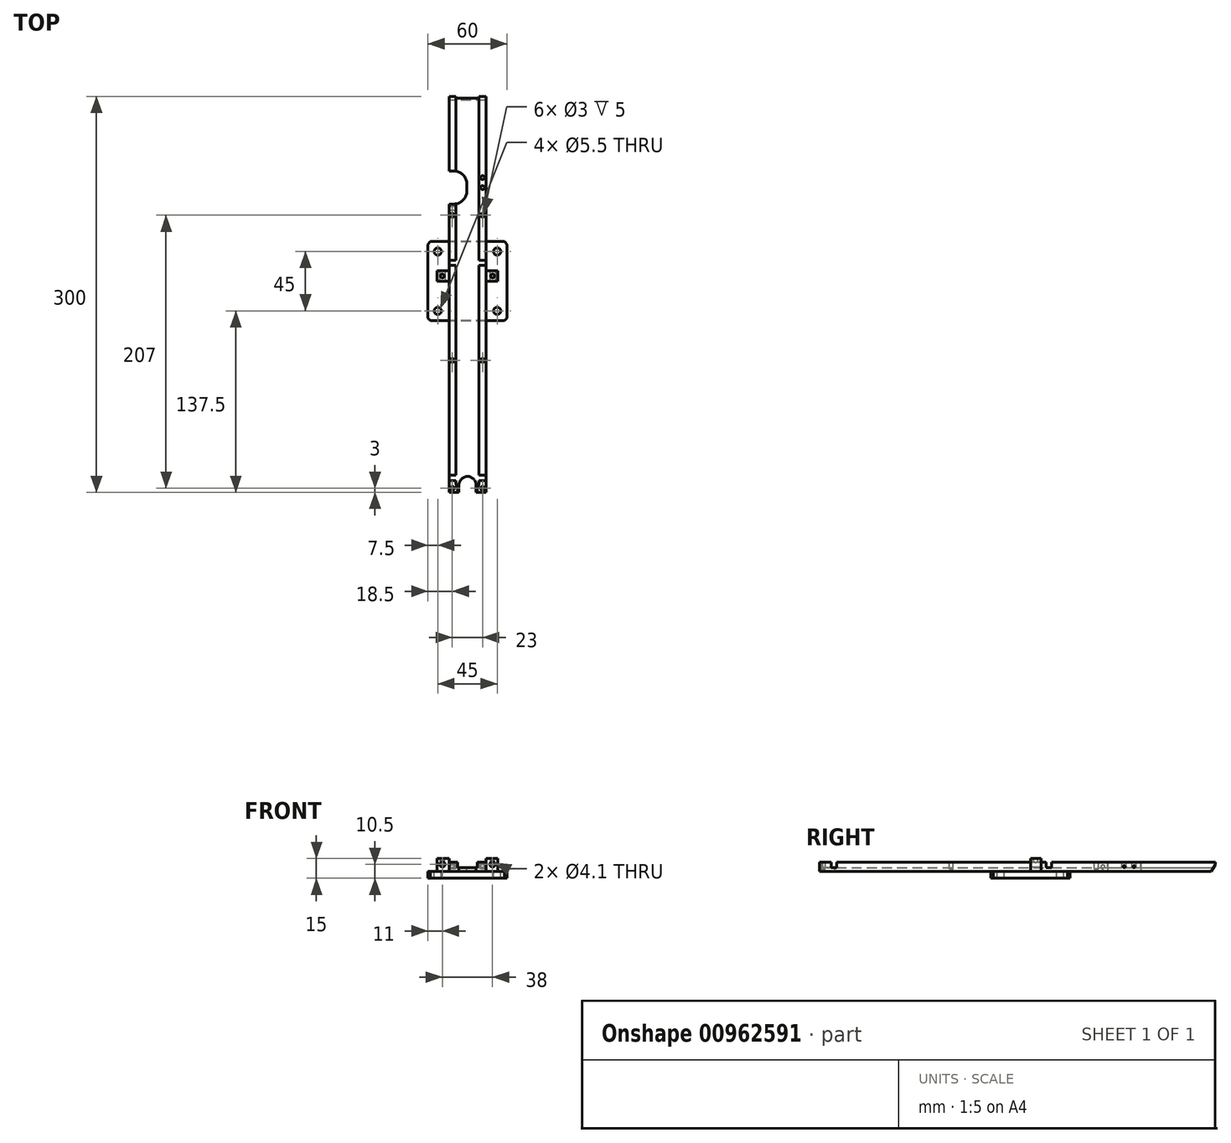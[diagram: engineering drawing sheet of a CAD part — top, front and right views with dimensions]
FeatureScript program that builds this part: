
annotation { "Feature Type Name" : "Feature", "Feature Type Description" : "" }
export const myFeature = defineFeature(function(context is Context, id is Id, definition is map)
    precondition{}
    {
        {
            var Q0;
            Q0=qCreatedBy(makeId("Front.planeOp"),FACE);
            var sketch = newSketch(context, id + "F0", { "sketchPlane" : qUnion([Q0])});
            skLineSegment(sketch, "E0.bottom", {"start": v(-30, 2.5) * mm, "end": v(-14, 2.5) * mm});
            skLineSegment(sketch, "E0.top", {"start": v(-30, -2.5) * mm, "end": v(30, -2.5) * mm});
            skLineSegment(sketch, "E0.left", {"start": v(-30, 2.5) * mm, "end": v(-30, -2.5) * mm});
            skLineSegment(sketch, "E0.right", {"start": v(30, 2.5) * mm, "end": v(30, -2.5) * mm});
            skPoint(sketch, "E0.middle", {"position": v(0, 0) * mm});
            skLineSegment(sketch, "E1.bottom", {"start": v(-14, 9.5) * mm, "end": v(-8.7, 9.5) * mm});
            skLineSegment(sketch, "E1.left", {"start": v(-14, 9.5) * mm, "end": v(-14, 2.5) * mm});
            skLineSegment(sketch, "E1.right", {"start": v(14, 9.5) * mm, "end": v(14, 2.5) * mm});
            skLineSegment(sketch, "E2.0", {"start": v(-8.7, 5.5) * mm, "end": v(8.7, 5.5) * mm});
            skLineSegment(sketch, "E3.left", {"start": v(-8.7, 9.5) * mm, "end": v(-8.7, 5.5) * mm});
            skLineSegment(sketch, "E3.right", {"start": v(8.7, 9.5) * mm, "end": v(8.7, 5.5) * mm});
            skLineSegment(sketch, "E4.trimOffspring", {"start": v(8.7, 9.5) * mm, "end": v(14, 9.5) * mm});
            skLineSegment(sketch, "E5.trimOffspring", {"start": v(14, 2.5) * mm, "end": v(30, 2.5) * mm});
            skSolve(sketch);
        }
        {
            var Q0;
            Q0=qSketchRegion(id+"F0",true);
            extrude(context, id + "F1", {"entities" : qUnion([Q0]), "depth" : 60 * mm, "offsetDistance" : 25 * mm});
        }
        {
            var Q0;
            Q0=makeQuery(id+"F1.opExtrude","CAP_FACE",FACE,{"disambiguationData":[OSD([sQuery(id+"F0.wireOp",EDGE,"E0.bottom"),sQuery(id+"F0.wireOp",EDGE,"E0.top"),sQuery(id+"F0.wireOp",EDGE,"E0.left"),sQuery(id+"F0.wireOp",EDGE,"E0.right"),sQuery(id+"F0.wireOp",EDGE,"E1.bottom"),sQuery(id+"F0.wireOp",EDGE,"E1.left"),sQuery(id+"F0.wireOp",EDGE,"E1.right"),sQuery(id+"F0.wireOp",EDGE,"E2.0"),sQuery(id+"F0.wireOp",EDGE,"E3.left"),sQuery(id+"F0.wireOp",EDGE,"E3.right"),sQuery(id+"F0.wireOp",EDGE,"E4.trimOffspring"),sQuery(id+"F0.wireOp",EDGE,"E5.trimOffspring")])],"isStart":false});
            var sketch = newSketch(context, id + "F2", { "sketchPlane" : qUnion([Q0])});
            skLineSegment(sketch, "E6.0.0", {"start": v(14, 9.5) * mm, "end": v(8.7, 9.5) * mm});
            skLineSegment(sketch, "E6.0.1", {"start": v(8.7, 9.5) * mm, "end": v(8.7, 5.5) * mm});
            skLineSegment(sketch, "E6.0.2", {"start": v(8.7, 5.5) * mm, "end": v(-8.7, 5.5) * mm});
            skLineSegment(sketch, "E6.0.3", {"start": v(-8.7, 5.5) * mm, "end": v(-8.7, 9.5) * mm});
            skLineSegment(sketch, "E6.0.4", {"start": v(-8.7, 9.5) * mm, "end": v(-14, 9.5) * mm});
            skLineSegment(sketch, "E6.0.5", {"start": v(-14, 9.5) * mm, "end": v(-14, 2.5) * mm});
            skLineSegment(sketch, "E6.0.11", {"start": v(14, 2.5) * mm, "end": v(14, 9.5) * mm});
            skPoint(sketch, "E6.0.7.start.orphan", {"position": v(-30, 2.5) * mm});
            skPoint(sketch, "E6.0.8.start.orphan", {"position": v(-30, -2.5) * mm});
            skPoint(sketch, "E6.0.9.start.orphan", {"position": v(30, -2.5) * mm});
            skPoint(sketch, "E6.0.10.start.orphan", {"position": v(30, 2.5) * mm});
            skLineSegment(sketch, "E7", {"start": v(14, 2.5) * mm, "end": v(-14, 2.5) * mm});
            skSolve(sketch);
        }
        {
            var Q0;
            Q0=qSketchRegion(id+"F2",true);
            extrude(context, id + "F3", {"entities" : qUnion([Q0]), "operationType" : NewBodyOperationType.ADD, "depth" : 130 * mm, "offsetDistance" : 25 * mm});
        }
        {
            var Q0;
            Q0=makeQuery(id+"F1.opExtrude","CAP_FACE",FACE,{"disambiguationData":[OSD([sQuery(id+"F0.wireOp",EDGE,"E0.bottom"),sQuery(id+"F0.wireOp",EDGE,"E0.top"),sQuery(id+"F0.wireOp",EDGE,"E0.left"),sQuery(id+"F0.wireOp",EDGE,"E0.right"),sQuery(id+"F0.wireOp",EDGE,"E1.bottom"),sQuery(id+"F0.wireOp",EDGE,"E1.left"),sQuery(id+"F0.wireOp",EDGE,"E1.right"),sQuery(id+"F0.wireOp",EDGE,"E2.0"),sQuery(id+"F0.wireOp",EDGE,"E3.left"),sQuery(id+"F0.wireOp",EDGE,"E3.right"),sQuery(id+"F0.wireOp",EDGE,"E4.trimOffspring"),sQuery(id+"F0.wireOp",EDGE,"E5.trimOffspring")])],"isStart":true});
            var sketch = newSketch(context, id + "F4", { "sketchPlane" : qUnion([Q0])});
            skLineSegment(sketch, "E8.0.0", {"start": v(-8.7, 9.5) * mm, "end": v(-14, 9.5) * mm});
            skLineSegment(sketch, "E8.0.1", {"start": v(-14, 9.5) * mm, "end": v(-14, 2.5) * mm});
            skLineSegment(sketch, "E8.0.7", {"start": v(14, 2.5) * mm, "end": v(14, 9.5) * mm});
            skLineSegment(sketch, "E8.0.8", {"start": v(14, 9.5) * mm, "end": v(8.7, 9.5) * mm});
            skLineSegment(sketch, "E8.0.9", {"start": v(8.7, 9.5) * mm, "end": v(8.7, 5.5) * mm});
            skLineSegment(sketch, "E8.0.10", {"start": v(8.7, 5.5) * mm, "end": v(-8.7, 5.5) * mm});
            skLineSegment(sketch, "E8.0.11", {"start": v(-8.7, 5.5) * mm, "end": v(-8.7, 9.5) * mm});
            skLineSegment(sketch, "E9", {"start": v(-14, 2.5) * mm, "end": v(14, 2.5) * mm});
            skPoint(sketch, "E8.0.3.start.orphan", {"position": v(-30, 2.5) * mm});
            skPoint(sketch, "E8.0.4.start.orphan", {"position": v(-30, -2.5) * mm});
            skPoint(sketch, "E8.0.5.start.orphan", {"position": v(30, -2.5) * mm});
            skPoint(sketch, "E8.0.6.start.orphan", {"position": v(30, 2.5) * mm});
            skSolve(sketch);
        }
        {
            var Q0;
            Q0=qSketchRegion(id+"F4",true);
            extrude(context, id + "F5", {"entities" : qUnion([Q0]), "operationType" : NewBodyOperationType.ADD, "depth" : 110 * mm, "offsetDistance" : 25 * mm});
        }
        {
            var Q0;
            Q0=makeQuery(id+"F1.opExtrude","SWEPT_FACE",FACE,{"disambiguationData":[OSD([sQuery(id+"F0.wireOp",EDGE,"E0.bottom")])]});
            var sketch = newSketch(context, id + "F6", { "sketchPlane" : qUnion([Q0])});
            skCircle(sketch, "E10", {"center": v(-22.5, -7.5) * mm, "radius": 2.75 * mm});
            skCircle(sketch, "E11.MirrorC", {"center": v(22.5, -7.5) * mm, "radius": 2.75 * mm});
            skCircle(sketch, "E12", {"center": v(-22.5, -52.5) * mm, "radius": 2.75 * mm});
            skCircle(sketch, "E13", {"center": v(22.5, -52.5) * mm, "radius": 2.75 * mm});
            skSolve(sketch);
        }
        {
            var Q0;
            Q0=qSketchRegion(id+"F6",true);
            extrude(context, id + "F7", {"entities" : qUnion([Q0]), "operationType" : NewBodyOperationType.REMOVE, "endBound" : BoundingType.THROUGH_ALL, "oppositeDirection" : true, "depth" : 25 * mm, "offsetDistance" : 25 * mm});
        }
        {
            var Q0;
            Q0=makeQuery(id+"F1.opExtrude","SWEPT_FACE",FACE,{"disambiguationData":[OSD([sQuery(id+"F0.wireOp",EDGE,"E0.bottom")])]});
            var sketch = newSketch(context, id + "F8", { "sketchPlane" : qUnion([Q0])});
            skLineSegment(sketch, "E14.bottom", {"start": v(-14, -22) * mm, "end": v(-23, -22) * mm});
            skLineSegment(sketch, "E14.top", {"start": v(-14, -30) * mm, "end": v(-23, -30) * mm});
            skLineSegment(sketch, "E14.left", {"start": v(-14, -22) * mm, "end": v(-14, -30) * mm});
            skLineSegment(sketch, "E14.right", {"start": v(-23, -22) * mm, "end": v(-23, -30) * mm});
            skLineSegment(sketch, "E15.MirrorCS", {"start": v(14, -22) * mm, "end": v(23, -22) * mm});
            skLineSegment(sketch, "E16.MirrorCS", {"start": v(14, -22) * mm, "end": v(14, -30) * mm});
            skLineSegment(sketch, "E17.MirrorCS", {"start": v(14, -30) * mm, "end": v(23, -30) * mm});
            skLineSegment(sketch, "E18.MirrorCS", {"start": v(23, -22) * mm, "end": v(23, -30) * mm});
            skSolve(sketch);
        }
        {
            var Q0;
            Q0=qSketchRegion(id+"F8",true);
            extrude(context, id + "F9", {"entities" : qUnion([Q0]), "operationType" : NewBodyOperationType.ADD, "depth" : 10 * mm, "offsetDistance" : 25 * mm});
        }
        {
            var Q0;
            Q0=makeQuery(id+"F9.opExtrude","CAP_FACE",FACE,{"disambiguationData":[OSD([sQuery(id+"F8.wireOp",EDGE,"E14.bottom"),sQuery(id+"F8.wireOp",EDGE,"E14.top"),sQuery(id+"F8.wireOp",EDGE,"E14.left"),sQuery(id+"F8.wireOp",EDGE,"E14.right")])],"isStart":false});
            var sketch = newSketch(context, id + "F10", { "sketchPlane" : qUnion([Q0])});
            skCircle(sketch, "E19", {"center": v(-19, -26) * mm, "radius": 1.5 * mm});
            skCircle(sketch, "E20.MirrorC", {"center": v(19, -26) * mm, "radius": 1.5 * mm});
            skSolve(sketch);
        }
        {
            var Q0;
            Q0=qSketchRegion(id+"F10",true);
            extrude(context, id + "F11", {"entities" : qUnion([Q0]), "operationType" : NewBodyOperationType.REMOVE, "oppositeDirection" : true, "depth" : 4.5 * mm, "offsetDistance" : 25 * mm});
        }
        {
            var Q0;
            Q0=makeQuery(id+"F9.opExtrude","SWEPT_FACE",FACE,{"disambiguationData":[OSD([sQuery(id+"F8.wireOp",EDGE,"E14.top")])]});
            var sketch = newSketch(context, id + "F12", { "sketchPlane" : qUnion([Q0])});
            skCircle(sketch, "E21", {"center": v(-19, 8) * mm, "radius": 2.05 * mm});
            skCircle(sketch, "E22", {"center": v(19, 8) * mm, "radius": 2.05 * mm});
            skSolve(sketch);
        }
        {
            var Q0;
            Q0=qSketchRegion(id+"F12",true);
            extrude(context, id + "F13", {"entities" : qUnion([Q0]), "operationType" : NewBodyOperationType.REMOVE, "endBound" : BoundingType.THROUGH_ALL, "oppositeDirection" : true, "depth" : 25 * mm, "offsetDistance" : 25 * mm});
        }
        {
            var Q0;
            Q0=makeQuery(id+"F1.opExtrude","CAP_EDGE",EDGE,{"disambiguationData":[OSD([sQuery(id+"F0.wireOp",EDGE,"E0.left")])],"isStart":false});
            var Q1;
            Q1=makeQuery(id+"F1.opExtrude","CAP_EDGE",EDGE,{"disambiguationData":[OSD([sQuery(id+"F0.wireOp",EDGE,"E0.right")])],"isStart":false});
            var Q2;
            Q2=makeQuery(id+"F1.opExtrude","CAP_EDGE",EDGE,{"disambiguationData":[OSD([sQuery(id+"F0.wireOp",EDGE,"E0.right")])],"isStart":true});
            var Q3;
            Q3=makeQuery(id+"F1.opExtrude","CAP_EDGE",EDGE,{"disambiguationData":[OSD([sQuery(id+"F0.wireOp",EDGE,"E0.left")])],"isStart":true});
            chamfer(context, id + "F14", {"entities" : qUnion([Q0, Q1, Q2, Q3]), "width" : 2 * mm, "tangentPropagation" : true});
        }
        {
            var Q0;
            {var subQ1=sQuery(id+"F0.wireOp",EDGE,"E1.left");var subQ4=sQuery(id+"F4.wireOp",EDGE,"E9");var subQ5=sQuery(id+"F4.wireOp",EDGE,"E8.0.7");Q0=makeQuery(id+"F9.boolean.opBoolean","SPLIT",FACE,{"disambiguationData":[TD([makeQuery(id+"F5.opExtrude","SWEPT_FACE",FACE,{"disambiguationData":[OSD([subQ4])]})])],"derivedFrom":makeQuery(id+"F5.boolean.opBoolean","MERGE",FACE,{"derivedFrom":[makeQuery(id+"F3.boolean.opBoolean","MERGE",FACE,{"derivedFrom":[makeQuery(id+"F1.opExtrude","SWEPT_FACE",FACE,{"disambiguationData":[OSD([subQ1])]}),makeQuery(id+"F3.opExtrude","SWEPT_FACE",FACE,{"disambiguationData":[OSD([sQuery(id+"F2.wireOp",EDGE,"E6.0.5")])]})]}),makeQuery(id+"F5.opExtrude","SWEPT_FACE",FACE,{"disambiguationData":[OSD([subQ5])]})]})});}
            var sketch = newSketch(context, id + "F15", { "sketchPlane" : qUnion([Q0])});
            skLineSegment(sketch, "E23.bottom", {"start": v(14, 9.5) * mm, "end": v(18, 9.5) * mm});
            skLineSegment(sketch, "E23.top", {"start": v(14, 5.5) * mm, "end": v(18, 5.5) * mm});
            skLineSegment(sketch, "E23.left", {"start": v(14, 9.5) * mm, "end": v(14, 5.5) * mm});
            skLineSegment(sketch, "E23.right", {"start": v(18, 9.5) * mm, "end": v(18, 5.5) * mm});
            skLineSegment(sketch, "E24.bottom", {"start": v(177, 9.5) * mm, "end": v(181, 9.5) * mm});
            skLineSegment(sketch, "E24.top", {"start": v(177, 5.5) * mm, "end": v(181, 5.5) * mm});
            skLineSegment(sketch, "E24.left", {"start": v(177, 9.5) * mm, "end": v(177, 5.5) * mm});
            skLineSegment(sketch, "E24.right", {"start": v(181, 9.5) * mm, "end": v(181, 5.5) * mm});
            skSolve(sketch);
        }
        {
            var Q0;
            Q0=qSketchRegion(id+"F15",true);
            extrude(context, id + "F16", {"entities" : qUnion([Q0]), "operationType" : NewBodyOperationType.REMOVE, "endBound" : BoundingType.THROUGH_ALL, "oppositeDirection" : true, "depth" : 25 * mm, "offsetDistance" : 25 * mm});
        }
        {
            var Q0;
            {var subQ1=sQuery(id+"F0.wireOp",EDGE,"E1.left");var subQ4=sQuery(id+"F4.wireOp",EDGE,"E9");var subQ5=sQuery(id+"F4.wireOp",EDGE,"E8.0.7");Q0=makeQuery(id+"F9.boolean.opBoolean","SPLIT",FACE,{"disambiguationData":[TD([makeQuery(id+"F5.opExtrude","SWEPT_FACE",FACE,{"disambiguationData":[OSD([subQ4])]})])],"derivedFrom":makeQuery(id+"F5.boolean.opBoolean","MERGE",FACE,{"derivedFrom":[makeQuery(id+"F3.boolean.opBoolean","MERGE",FACE,{"derivedFrom":[makeQuery(id+"F1.opExtrude","SWEPT_FACE",FACE,{"disambiguationData":[OSD([subQ1])]}),makeQuery(id+"F3.opExtrude","SWEPT_FACE",FACE,{"disambiguationData":[OSD([sQuery(id+"F2.wireOp",EDGE,"E6.0.5")])]})]}),makeQuery(id+"F5.opExtrude","SWEPT_FACE",FACE,{"disambiguationData":[OSD([subQ5])]})]})});}
            var sketch = newSketch(context, id + "F17", { "sketchPlane" : qUnion([Q0])});
            skLineSegment(sketch, "E25", {"start": v(-110, 7.7) * mm, "end": v(-107, 2.5) * mm});
            skLineSegment(sketch, "E26", {"start": v(-107, 2.5) * mm, "end": v(-110, 2.5) * mm});
            skLineSegment(sketch, "E27", {"start": v(-110, 2.5) * mm, "end": v(-110, 7.7) * mm});
            skSolve(sketch);
        }
        {
            var Q0;
            Q0=qSketchRegion(id+"F17",true);
            extrude(context, id + "F18", {"entities" : qUnion([Q0]), "operationType" : NewBodyOperationType.REMOVE, "endBound" : BoundingType.THROUGH_ALL, "oppositeDirection" : true, "depth" : 25 * mm, "offsetDistance" : 25 * mm});
        }
        {
            var Q0;
            Q0=makeQuery(id+"F16.boolean.opBoolean","MERGE",FACE,{"derivedFrom":[makeQuery(id+"F5.boolean.opBoolean","MERGE",FACE,{"derivedFrom":[makeQuery(id+"F3.boolean.opBoolean","MERGE",FACE,{"derivedFrom":[makeQuery(id+"F1.opExtrude","SWEPT_FACE",FACE,{"disambiguationData":[OSD([sQuery(id+"F0.wireOp",EDGE,"E2.0")])]}),makeQuery(id+"F3.opExtrude","SWEPT_FACE",FACE,{"disambiguationData":[OSD([sQuery(id+"F2.wireOp",EDGE,"E6.0.2")])]})]}),makeQuery(id+"F5.opExtrude","SWEPT_FACE",FACE,{"disambiguationData":[OSD([sQuery(id+"F4.wireOp",EDGE,"E8.0.10")])]})]}),makeQuery(id+"F16.opExtrude","SWEPT_FACE",FACE,{"disambiguationData":[OSD([sQuery(id+"F15.wireOp",EDGE,"E23.top")])]}),makeQuery(id+"F16.opExtrude","SWEPT_FACE",FACE,{"disambiguationData":[OSD([sQuery(id+"F15.wireOp",EDGE,"E24.top")])]})]});
            var sketch = newSketch(context, id + "F19", { "sketchPlane" : qUnion([Q0])});
            skLineSegment(sketch, "E28.bottom", {"start": v(8.7, -190) * mm, "end": v(-8.7, -190) * mm});
            skLineSegment(sketch, "E28.top", {"start": v(8.7, -175) * mm, "end": v(-8.7, -175) * mm});
            skLineSegment(sketch, "E28.left", {"start": v(8.7, -190) * mm, "end": v(8.7, -175) * mm});
            skLineSegment(sketch, "E28.right", {"start": v(-8.7, -190) * mm, "end": v(-8.7, -175) * mm});
            skSolve(sketch);
        }
        {
            var Q0;
            Q0=qSketchRegion(id+"F19",true);
            var Q1;
            {var subQ2=sQuery(id+"F2.wireOp",EDGE,"E6.0.4");Q1=makeQuery(id+"F16.boolean.opBoolean","SPLIT",FACE,{"disambiguationData":[TD([makeQuery(id+"F16.opExtrude","SWEPT_FACE",FACE,{"disambiguationData":[OSD([sQuery(id+"F15.wireOp",EDGE,"E24.right")])]})])],"derivedFrom":makeQuery(id+"F5.boolean.opBoolean","MERGE",FACE,{"derivedFrom":[makeQuery(id+"F3.boolean.opBoolean","MERGE",FACE,{"derivedFrom":[makeQuery(id+"F1.opExtrude","SWEPT_FACE",FACE,{"disambiguationData":[OSD([sQuery(id+"F0.wireOp",EDGE,"E1.bottom")])]}),makeQuery(id+"F3.opExtrude","SWEPT_FACE",FACE,{"disambiguationData":[OSD([subQ2])]})]}),makeQuery(id+"F5.opExtrude","SWEPT_FACE",FACE,{"disambiguationData":[OSD([sQuery(id+"F4.wireOp",EDGE,"E8.0.8")])]})]})});}
            extrude(context, id + "F20", {"entities" : qUnion([Q0]), "operationType" : NewBodyOperationType.ADD, "endBound" : BoundingType.UP_TO_SURFACE, "depth" : 25 * mm, "endBoundEntityFace" : qUnion([Q1]), "offsetDistance" : 25 * mm});
        }
        {
            var Q0;
            {var subQ10=sQuery(id+"F2.wireOp",EDGE,"E6.0.0");var subQ11=makeQuery(id+"F5.boolean.opBoolean","MERGE",FACE,{"derivedFrom":[makeQuery(id+"F3.boolean.opBoolean","MERGE",FACE,{"derivedFrom":[makeQuery(id+"F1.opExtrude","SWEPT_FACE",FACE,{"disambiguationData":[OSD([sQuery(id+"F0.wireOp",EDGE,"E4.trimOffspring")])]}),makeQuery(id+"F3.opExtrude","SWEPT_FACE",FACE,{"disambiguationData":[OSD([subQ10])]})]}),makeQuery(id+"F5.opExtrude","SWEPT_FACE",FACE,{"disambiguationData":[OSD([sQuery(id+"F4.wireOp",EDGE,"E8.0.0")])]})]});var subQ13=sQuery(id+"F2.wireOp",EDGE,"E6.0.4");var subQ16=makeQuery(id+"F16.opExtrude","SWEPT_FACE",FACE,{"disambiguationData":[OSD([sQuery(id+"F15.wireOp",EDGE,"E24.right")])]});var subQ23=makeQuery(id+"F5.boolean.opBoolean","MERGE",FACE,{"derivedFrom":[makeQuery(id+"F3.boolean.opBoolean","MERGE",FACE,{"derivedFrom":[makeQuery(id+"F1.opExtrude","SWEPT_FACE",FACE,{"disambiguationData":[OSD([sQuery(id+"F0.wireOp",EDGE,"E1.bottom")])]}),makeQuery(id+"F3.opExtrude","SWEPT_FACE",FACE,{"disambiguationData":[OSD([subQ13])]})]}),makeQuery(id+"F5.opExtrude","SWEPT_FACE",FACE,{"disambiguationData":[OSD([sQuery(id+"F4.wireOp",EDGE,"E8.0.8")])]})]});Q0=makeQuery(id+"F20.boolean.opBoolean","MERGE",FACE,{"derivedFrom":[makeQuery(id+"F16.boolean.opBoolean","SPLIT",FACE,{"disambiguationData":[TD([subQ16])],"derivedFrom":subQ23}),makeQuery(id+"F16.boolean.opBoolean","SPLIT",FACE,{"disambiguationData":[TD([makeQuery(id+"F9.opExtrude","SWEPT_FACE",FACE,{"disambiguationData":[OSD([sQuery(id+"F8.wireOp",EDGE,"E14.bottom")])]})])],"derivedFrom":subQ23}),makeQuery(id+"F16.boolean.opBoolean","SPLIT",FACE,{"disambiguationData":[TD([subQ16])],"derivedFrom":subQ11}),makeQuery(id+"F16.boolean.opBoolean","SPLIT",FACE,{"disambiguationData":[TD([makeQuery(id+"F9.opExtrude","SWEPT_FACE",FACE,{"disambiguationData":[OSD([sQuery(id+"F8.wireOp",EDGE,"E15.MirrorCS")])]})])],"derivedFrom":subQ11}),makeQuery(id+"F20.opExtrude","CAP_FACE",FACE,{"disambiguationData":[OSD([sQuery(id+"F19.wireOp",EDGE,"E28.bottom"),sQuery(id+"F19.wireOp",EDGE,"E28.top"),sQuery(id+"F19.wireOp",EDGE,"E28.left"),sQuery(id+"F19.wireOp",EDGE,"E28.right")])],"isStart":false})]});}
            var sketch = newSketch(context, id + "F21", { "sketchPlane" : qUnion([Q0])});
            skLineSegment(sketch, "E29.bottom", {"start": v(6.5, -190) * mm, "end": v(-6.5, -190) * mm});
            skLineSegment(sketch, "E29.left", {"start": v(6.5, -190) * mm, "end": v(6.5, -184.5) * mm});
            skLineSegment(sketch, "E29.right", {"start": v(-6.5, -190) * mm, "end": v(-6.5, -184.5) * mm});
            skPoint(sketch, "E30.endSnap0", {"position": v(0, -190) * mm});
            skArc(sketch, "E31", {"start": v(6.5, -184.5) * mm, "mid": v(0, -178) * mm, "end": v(-6.5, -184.5) * mm});
            skPoint(sketch, "E32.orphan", {"position": v(0, -183) * mm});
            skPoint(sketch, "E30.start.orphan", {"position": v(0, -190) * mm});
            skSolve(sketch);
        }
        {
            var Q0;
            Q0=qSketchRegion(id+"F21",true);
            extrude(context, id + "F22", {"entities" : qUnion([Q0]), "operationType" : NewBodyOperationType.REMOVE, "endBound" : BoundingType.THROUGH_ALL, "oppositeDirection" : true, "depth" : 25 * mm, "offsetDistance" : 25 * mm});
        }
        {
            var Q0;
            {var subQ10=sQuery(id+"F2.wireOp",EDGE,"E6.0.0");var subQ11=makeQuery(id+"F5.boolean.opBoolean","MERGE",FACE,{"derivedFrom":[makeQuery(id+"F3.boolean.opBoolean","MERGE",FACE,{"derivedFrom":[makeQuery(id+"F1.opExtrude","SWEPT_FACE",FACE,{"disambiguationData":[OSD([sQuery(id+"F0.wireOp",EDGE,"E4.trimOffspring")])]}),makeQuery(id+"F3.opExtrude","SWEPT_FACE",FACE,{"disambiguationData":[OSD([subQ10])]})]}),makeQuery(id+"F5.opExtrude","SWEPT_FACE",FACE,{"disambiguationData":[OSD([sQuery(id+"F4.wireOp",EDGE,"E8.0.0")])]})]});var subQ13=sQuery(id+"F2.wireOp",EDGE,"E6.0.4");var subQ16=makeQuery(id+"F16.opExtrude","SWEPT_FACE",FACE,{"disambiguationData":[OSD([sQuery(id+"F15.wireOp",EDGE,"E24.right")])]});var subQ23=makeQuery(id+"F5.boolean.opBoolean","MERGE",FACE,{"derivedFrom":[makeQuery(id+"F3.boolean.opBoolean","MERGE",FACE,{"derivedFrom":[makeQuery(id+"F1.opExtrude","SWEPT_FACE",FACE,{"disambiguationData":[OSD([sQuery(id+"F0.wireOp",EDGE,"E1.bottom")])]}),makeQuery(id+"F3.opExtrude","SWEPT_FACE",FACE,{"disambiguationData":[OSD([subQ13])]})]}),makeQuery(id+"F5.opExtrude","SWEPT_FACE",FACE,{"disambiguationData":[OSD([sQuery(id+"F4.wireOp",EDGE,"E8.0.8")])]})]});Q0=makeQuery(id+"F20.boolean.opBoolean","MERGE",FACE,{"derivedFrom":[makeQuery(id+"F16.boolean.opBoolean","SPLIT",FACE,{"disambiguationData":[TD([subQ16])],"derivedFrom":subQ23}),makeQuery(id+"F16.boolean.opBoolean","SPLIT",FACE,{"disambiguationData":[TD([makeQuery(id+"F9.opExtrude","SWEPT_FACE",FACE,{"disambiguationData":[OSD([sQuery(id+"F8.wireOp",EDGE,"E14.bottom")])]})])],"derivedFrom":subQ23}),makeQuery(id+"F16.boolean.opBoolean","SPLIT",FACE,{"disambiguationData":[TD([subQ16])],"derivedFrom":subQ11}),makeQuery(id+"F16.boolean.opBoolean","SPLIT",FACE,{"disambiguationData":[TD([makeQuery(id+"F9.opExtrude","SWEPT_FACE",FACE,{"disambiguationData":[OSD([sQuery(id+"F8.wireOp",EDGE,"E15.MirrorCS")])]})])],"derivedFrom":subQ11}),makeQuery(id+"F20.opExtrude","CAP_FACE",FACE,{"disambiguationData":[OSD([sQuery(id+"F19.wireOp",EDGE,"E28.bottom"),sQuery(id+"F19.wireOp",EDGE,"E28.top"),sQuery(id+"F19.wireOp",EDGE,"E28.left"),sQuery(id+"F19.wireOp",EDGE,"E28.right")])],"isStart":false})]});}
            var sketch = newSketch(context, id + "F23", { "sketchPlane" : qUnion([Q0])});
            skCircle(sketch, "E33", {"center": v(0, -183) * mm, "radius": 8.7 * mm});
            skPoint(sketch, "E33.centerSnap0", {"position": v(0, -175) * mm});
            skSolve(sketch);
        }
        {
            var Q0;
            Q0=qSketchRegion(id+"F23",true);
            var Q1;
            {var subQ9=makeQuery(id+"F1.opExtrude","SWEPT_FACE",FACE,{"disambiguationData":[OSD([sQuery(id+"F0.wireOp",EDGE,"E3.left")])]});var subQ13=makeQuery(id+"F3.opExtrude","SWEPT_FACE",FACE,{"disambiguationData":[OSD([sQuery(id+"F2.wireOp",EDGE,"E6.0.2")])]});var subQ14=makeQuery(id+"F16.opExtrude","SWEPT_FACE",FACE,{"disambiguationData":[OSD([sQuery(id+"F15.wireOp",EDGE,"E24.top")])]});var subQ15=makeQuery(id+"F1.opExtrude","SWEPT_FACE",FACE,{"disambiguationData":[OSD([sQuery(id+"F0.wireOp",EDGE,"E2.0")])]});var subQ18=makeQuery(id+"F5.opExtrude","SWEPT_FACE",FACE,{"disambiguationData":[OSD([sQuery(id+"F4.wireOp",EDGE,"E8.0.10")])]});var subQ19=makeQuery(id+"F16.opExtrude","SWEPT_FACE",FACE,{"disambiguationData":[OSD([sQuery(id+"F15.wireOp",EDGE,"E23.top")])]});Q1=makeQuery(id+"F20.boolean.opBoolean","SPLIT",FACE,{"disambiguationData":[TD([subQ9])],"derivedFrom":makeQuery(id+"F16.boolean.opBoolean","MERGE",FACE,{"derivedFrom":[makeQuery(id+"F5.boolean.opBoolean","MERGE",FACE,{"derivedFrom":[makeQuery(id+"F3.boolean.opBoolean","MERGE",FACE,{"derivedFrom":[subQ15,subQ13]}),subQ18]}),subQ19,subQ14]})});}
            extrude(context, id + "F24", {"entities" : qUnion([Q0]), "operationType" : NewBodyOperationType.REMOVE, "endBound" : BoundingType.UP_TO_SURFACE, "oppositeDirection" : true, "depth" : 25 * mm, "endBoundEntityFace" : qUnion([Q1]), "offsetDistance" : 25 * mm});
        }
        {
            var Q0;
            {var subQ9=makeQuery(id+"F1.opExtrude","SWEPT_FACE",FACE,{"disambiguationData":[OSD([sQuery(id+"F0.wireOp",EDGE,"E3.left")])]});var subQ13=makeQuery(id+"F3.opExtrude","SWEPT_FACE",FACE,{"disambiguationData":[OSD([sQuery(id+"F2.wireOp",EDGE,"E6.0.2")])]});var subQ14=makeQuery(id+"F16.opExtrude","SWEPT_FACE",FACE,{"disambiguationData":[OSD([sQuery(id+"F15.wireOp",EDGE,"E24.top")])]});var subQ15=makeQuery(id+"F1.opExtrude","SWEPT_FACE",FACE,{"disambiguationData":[OSD([sQuery(id+"F0.wireOp",EDGE,"E2.0")])]});var subQ18=makeQuery(id+"F5.opExtrude","SWEPT_FACE",FACE,{"disambiguationData":[OSD([sQuery(id+"F4.wireOp",EDGE,"E8.0.10")])]});var subQ19=makeQuery(id+"F16.opExtrude","SWEPT_FACE",FACE,{"disambiguationData":[OSD([sQuery(id+"F15.wireOp",EDGE,"E23.top")])]});Q0=makeQuery(id+"F24.boolean.opBoolean","MERGE",FACE,{"derivedFrom":[makeQuery(id+"F20.boolean.opBoolean","SPLIT",FACE,{"disambiguationData":[TD([subQ9])],"derivedFrom":makeQuery(id+"F16.boolean.opBoolean","MERGE",FACE,{"derivedFrom":[makeQuery(id+"F5.boolean.opBoolean","MERGE",FACE,{"derivedFrom":[makeQuery(id+"F3.boolean.opBoolean","MERGE",FACE,{"derivedFrom":[subQ15,subQ13]}),subQ18]}),subQ19,subQ14]})}),makeQuery(id+"F24.opExtrude","CAP_FACE",FACE,{"disambiguationData":[OSD([sQuery(id+"F23.wireOp",EDGE,"E33")])],"isStart":false})]});}
            var sketch = newSketch(context, id + "F25", { "sketchPlane" : qUnion([Q0])});
            skLineSegment(sketch, "E34.bottom", {"start": v(8.7, -175) * mm, "end": v(-8.7, -175) * mm});
            skLineSegment(sketch, "E34.top", {"start": v(8.7, -183) * mm, "end": v(-8.7, -183) * mm});
            skLineSegment(sketch, "E34.left", {"start": v(8.7, -175) * mm, "end": v(8.7, -183) * mm});
            skLineSegment(sketch, "E34.right", {"start": v(-8.7, -175) * mm, "end": v(-8.7, -183) * mm});
            skSolve(sketch);
        }
        {
            var Q0;
            Q0=qSketchRegion(id+"F25",true);
            var Q1;
            {var subQ1=makeQuery(id+"F1.opExtrude","SWEPT_FACE",FACE,{"disambiguationData":[OSD([sQuery(id+"F0.wireOp",EDGE,"E1.right")])]});var subQ5=makeQuery(id+"F9.opExtrude","SWEPT_FACE",FACE,{"disambiguationData":[OSD([sQuery(id+"F8.wireOp",EDGE,"E15.MirrorCS")])]});var subQ9=makeQuery(id+"F5.opExtrude","SWEPT_FACE",FACE,{"disambiguationData":[OSD([sQuery(id+"F4.wireOp",EDGE,"E8.0.0")])]});var subQ13=makeQuery(id+"F1.opExtrude","SWEPT_FACE",FACE,{"disambiguationData":[OSD([sQuery(id+"F0.wireOp",EDGE,"E4.trimOffspring")])]});var subQ15=sQuery(id+"F2.wireOp",EDGE,"E6.0.0");var subQ16=makeQuery(id+"F3.opExtrude","SWEPT_FACE",FACE,{"disambiguationData":[OSD([subQ15])]});var subQ23=sQuery(id+"F2.wireOp",EDGE,"E6.0.4");var subQ26=sQuery(id+"F19.wireOp",EDGE,"E28.left");var subQ27=sQuery(id+"F19.wireOp",EDGE,"E28.bottom");var subQ29=sQuery(id+"F19.wireOp",EDGE,"E28.top");var subQ30=makeQuery(id+"F16.opExtrude","SWEPT_FACE",FACE,{"disambiguationData":[OSD([sQuery(id+"F15.wireOp",EDGE,"E24.right")])]});var subQ31=makeQuery(id+"F5.boolean.opBoolean","MERGE",FACE,{"derivedFrom":[makeQuery(id+"F3.boolean.opBoolean","MERGE",FACE,{"derivedFrom":[subQ13,subQ16]}),subQ9]});var subQ38=makeQuery(id+"F5.boolean.opBoolean","MERGE",FACE,{"derivedFrom":[makeQuery(id+"F3.boolean.opBoolean","MERGE",FACE,{"derivedFrom":[makeQuery(id+"F1.opExtrude","SWEPT_FACE",FACE,{"disambiguationData":[OSD([sQuery(id+"F0.wireOp",EDGE,"E1.bottom")])]}),makeQuery(id+"F3.opExtrude","SWEPT_FACE",FACE,{"disambiguationData":[OSD([subQ23])]})]}),makeQuery(id+"F5.opExtrude","SWEPT_FACE",FACE,{"disambiguationData":[OSD([sQuery(id+"F4.wireOp",EDGE,"E8.0.8")])]})]});Q1=makeQuery(id+"F24.boolean.opBoolean","SPLIT",FACE,{"disambiguationData":[TD([subQ1])],"derivedFrom":makeQuery(id+"F20.boolean.opBoolean","MERGE",FACE,{"derivedFrom":[makeQuery(id+"F16.boolean.opBoolean","SPLIT",FACE,{"disambiguationData":[TD([subQ30])],"derivedFrom":subQ38}),makeQuery(id+"F16.boolean.opBoolean","SPLIT",FACE,{"disambiguationData":[TD([makeQuery(id+"F9.opExtrude","SWEPT_FACE",FACE,{"disambiguationData":[OSD([sQuery(id+"F8.wireOp",EDGE,"E14.bottom")])]})])],"derivedFrom":subQ38}),makeQuery(id+"F16.boolean.opBoolean","SPLIT",FACE,{"disambiguationData":[TD([subQ30])],"derivedFrom":subQ31}),makeQuery(id+"F16.boolean.opBoolean","SPLIT",FACE,{"disambiguationData":[TD([subQ5])],"derivedFrom":subQ31}),makeQuery(id+"F20.opExtrude","CAP_FACE",FACE,{"disambiguationData":[OSD([subQ27,subQ29,subQ26,sQuery(id+"F19.wireOp",EDGE,"E28.right")])],"isStart":false})]})});}
            extrude(context, id + "F26", {"entities" : qUnion([Q0]), "operationType" : NewBodyOperationType.REMOVE, "endBound" : BoundingType.UP_TO_SURFACE, "depth" : 25 * mm, "endBoundEntityFace" : qUnion([Q1]), "offsetDistance" : 25 * mm});
        }
        {
            var Q0;
            Q0=qCreatedBy(makeId("Right.planeOp"),FACE);
            var sketch = newSketch(context, id + "F27", { "sketchPlane" : qUnion([Q0])});
            skLineSegment(sketch, "E35.bottom", {"start": v(32, 6.5) * mm, "end": v(50, 6.5) * mm});
            skLineSegment(sketch, "E35.top", {"start": v(32, 5.5) * mm, "end": v(50, 5.5) * mm});
            skLineSegment(sketch, "E35.left", {"start": v(32, 6.5) * mm, "end": v(32, 5.5) * mm});
            skLineSegment(sketch, "E35.right", {"start": v(50, 6.5) * mm, "end": v(50, 5.5) * mm});
            skSolve(sketch);
        }
        {
            var Q0;
            Q0=qSketchRegion(id+"F27",true);
            extrude(context, id + "F28", {"entities" : qUnion([Q0]), "operationType" : NewBodyOperationType.REMOVE, "endBound" : BoundingType.THROUGH_ALL, "depth" : 10 * mm, "offsetDistance" : 25 * mm});
        }
        {
            var Q0;
            {var subQ9=makeQuery(id+"F1.opExtrude","SWEPT_FACE",FACE,{"disambiguationData":[OSD([sQuery(id+"F0.wireOp",EDGE,"E3.left")])]});var subQ13=makeQuery(id+"F3.opExtrude","SWEPT_FACE",FACE,{"disambiguationData":[OSD([sQuery(id+"F2.wireOp",EDGE,"E6.0.2")])]});var subQ14=makeQuery(id+"F16.opExtrude","SWEPT_FACE",FACE,{"disambiguationData":[OSD([sQuery(id+"F15.wireOp",EDGE,"E24.top")])]});var subQ15=makeQuery(id+"F1.opExtrude","SWEPT_FACE",FACE,{"disambiguationData":[OSD([sQuery(id+"F0.wireOp",EDGE,"E2.0")])]});var subQ18=makeQuery(id+"F5.opExtrude","SWEPT_FACE",FACE,{"disambiguationData":[OSD([sQuery(id+"F4.wireOp",EDGE,"E8.0.10")])]});var subQ19=makeQuery(id+"F16.opExtrude","SWEPT_FACE",FACE,{"disambiguationData":[OSD([sQuery(id+"F15.wireOp",EDGE,"E23.top")])]});var subQ25=makeQuery(id+"F16.boolean.opBoolean","MERGE",FACE,{"derivedFrom":[makeQuery(id+"F5.boolean.opBoolean","MERGE",FACE,{"derivedFrom":[makeQuery(id+"F3.boolean.opBoolean","MERGE",FACE,{"derivedFrom":[subQ15,subQ13]}),subQ18]}),subQ19,subQ14]});Q0=makeQuery(id+"F28.boolean.opBoolean","MERGE",FACE,{"derivedFrom":[makeQuery(id+"F26.boolean.opBoolean","MERGE",FACE,{"derivedFrom":[makeQuery(id+"F20.boolean.opBoolean","SPLIT",FACE,{"disambiguationData":[TD([makeQuery(id+"F20.opExtrude","SWEPT_FACE",FACE,{"disambiguationData":[OSD([sQuery(id+"F19.wireOp",EDGE,"E28.right")])]})])],"derivedFrom":subQ25}),makeQuery(id+"F20.boolean.opBoolean","SPLIT",FACE,{"disambiguationData":[TD([makeQuery(id+"F20.opExtrude","SWEPT_FACE",FACE,{"disambiguationData":[OSD([sQuery(id+"F19.wireOp",EDGE,"E28.left")])]})])],"derivedFrom":subQ25}),makeQuery(id+"F24.boolean.opBoolean","MERGE",FACE,{"derivedFrom":[makeQuery(id+"F20.boolean.opBoolean","SPLIT",FACE,{"disambiguationData":[TD([subQ9])],"derivedFrom":subQ25}),makeQuery(id+"F24.opExtrude","CAP_FACE",FACE,{"disambiguationData":[OSD([sQuery(id+"F23.wireOp",EDGE,"E33")])],"isStart":false})]}),makeQuery(id+"F26.opExtrude","CAP_FACE",FACE,{"disambiguationData":[OSD([sQuery(id+"F25.wireOp",EDGE,"E34.bottom"),sQuery(id+"F25.wireOp",EDGE,"E34.top"),sQuery(id+"F25.wireOp",EDGE,"E34.left"),sQuery(id+"F25.wireOp",EDGE,"E34.right")])],"isStart":true})]}),makeQuery(id+"F28.opExtrude","SWEPT_FACE",FACE,{"disambiguationData":[OSD([sQuery(id+"F27.wireOp",EDGE,"E35.top")])]})]});}
            var sketch = newSketch(context, id + "F29", { "sketchPlane" : qUnion([Q0])});
            skLineSegment(sketch, "E36.right", {"start": v(-14.2, 53.5) * mm, "end": v(-14.2, 34.9) * mm});
            skPoint(sketch, "E37.centerSnap0", {"position": v(-0.4, 41) * mm});
            skLineSegment(sketch, "E38", {"start": v(-14.2, 34.9) * mm, "end": v(-14.2, 53.5) * mm});
            skPoint(sketch, "E36.left.start.orphan", {"position": v(-0.4, 50) * mm});
            skPoint(sketch, "E39.trimOffspring.end.orphan", {"position": v(-0.4, 32) * mm});
            skLineSegment(sketch, "E40.bottom", {"start": v(-14.2, 53.5) * mm, "end": v(-0.4, 53.5) * mm});
            skLineSegment(sketch, "E40.top", {"start": v(-14.2, 28.5) * mm, "end": v(-0.4, 28.5) * mm});
            skLineSegment(sketch, "E40.left", {"start": v(-14.2, 53.5) * mm, "end": v(-14.2, 28.5) * mm});
            skLineSegment(sketch, "E40.right", {"start": v(-0.4, 53.5) * mm, "end": v(-0.4, 28.5) * mm});
            skSolve(sketch);
        }
        {
            var Q0;
            Q0=qSketchRegion(id+"F29",true);
            extrude(context, id + "F30", {"entities" : qUnion([Q0]), "operationType" : NewBodyOperationType.REMOVE, "endBound" : BoundingType.SYMMETRIC, "oppositeDirection" : true, "depth" : 30 * mm, "offsetDistance" : 25 * mm});
        }
        {
            var Q0;
            Q0=makeQuery(id+"F30.boolean.opBoolean","COPY",EDGE,{"derivedFrom":makeQuery(id+"F30.opExtrude","SWEPT_EDGE",EDGE,{"disambiguationData":[OSD([sQuery(id+"F29.wireOp",EDGE,"E40.bottom"),sQuery(id+"F29.wireOp",EDGE,"E40.right")])]})});
            var Q1;
            Q1=makeQuery(id+"F30.boolean.opBoolean","COPY",EDGE,{"derivedFrom":makeQuery(id+"F30.opExtrude","SWEPT_EDGE",EDGE,{"disambiguationData":[OSD([sQuery(id+"F29.wireOp",EDGE,"E40.top"),sQuery(id+"F29.wireOp",EDGE,"E40.right")])]})});
            fillet(context, id + "F31", {"entities" : qUnion([Q0, Q1]), "radius" : 10 * mm, "tangentPropagation" : true, "allowEdgeOverflow" : false});
        }
        {
            var Q0;
            {var subQ9=makeQuery(id+"F1.opExtrude","SWEPT_FACE",FACE,{"disambiguationData":[OSD([sQuery(id+"F0.wireOp",EDGE,"E3.left")])]});var subQ13=makeQuery(id+"F3.opExtrude","SWEPT_FACE",FACE,{"disambiguationData":[OSD([sQuery(id+"F2.wireOp",EDGE,"E6.0.2")])]});var subQ14=makeQuery(id+"F16.opExtrude","SWEPT_FACE",FACE,{"disambiguationData":[OSD([sQuery(id+"F15.wireOp",EDGE,"E24.top")])]});var subQ15=makeQuery(id+"F1.opExtrude","SWEPT_FACE",FACE,{"disambiguationData":[OSD([sQuery(id+"F0.wireOp",EDGE,"E2.0")])]});var subQ18=makeQuery(id+"F5.opExtrude","SWEPT_FACE",FACE,{"disambiguationData":[OSD([sQuery(id+"F4.wireOp",EDGE,"E8.0.10")])]});var subQ19=makeQuery(id+"F16.opExtrude","SWEPT_FACE",FACE,{"disambiguationData":[OSD([sQuery(id+"F15.wireOp",EDGE,"E23.top")])]});var subQ25=makeQuery(id+"F16.boolean.opBoolean","MERGE",FACE,{"derivedFrom":[makeQuery(id+"F5.boolean.opBoolean","MERGE",FACE,{"derivedFrom":[makeQuery(id+"F3.boolean.opBoolean","MERGE",FACE,{"derivedFrom":[subQ15,subQ13]}),subQ18]}),subQ19,subQ14]});Q0=makeQuery(id+"F28.boolean.opBoolean","MERGE",FACE,{"derivedFrom":[makeQuery(id+"F26.boolean.opBoolean","MERGE",FACE,{"derivedFrom":[makeQuery(id+"F20.boolean.opBoolean","SPLIT",FACE,{"disambiguationData":[TD([makeQuery(id+"F20.opExtrude","SWEPT_FACE",FACE,{"disambiguationData":[OSD([sQuery(id+"F19.wireOp",EDGE,"E28.right")])]})])],"derivedFrom":subQ25}),makeQuery(id+"F20.boolean.opBoolean","SPLIT",FACE,{"disambiguationData":[TD([makeQuery(id+"F20.opExtrude","SWEPT_FACE",FACE,{"disambiguationData":[OSD([sQuery(id+"F19.wireOp",EDGE,"E28.left")])]})])],"derivedFrom":subQ25}),makeQuery(id+"F24.boolean.opBoolean","MERGE",FACE,{"derivedFrom":[makeQuery(id+"F20.boolean.opBoolean","SPLIT",FACE,{"disambiguationData":[TD([subQ9])],"derivedFrom":subQ25}),makeQuery(id+"F24.opExtrude","CAP_FACE",FACE,{"disambiguationData":[OSD([sQuery(id+"F23.wireOp",EDGE,"E33")])],"isStart":false})]}),makeQuery(id+"F26.opExtrude","CAP_FACE",FACE,{"disambiguationData":[OSD([sQuery(id+"F25.wireOp",EDGE,"E34.bottom"),sQuery(id+"F25.wireOp",EDGE,"E34.top"),sQuery(id+"F25.wireOp",EDGE,"E34.left"),sQuery(id+"F25.wireOp",EDGE,"E34.right")])],"isStart":true})]}),makeQuery(id+"F28.opExtrude","SWEPT_FACE",FACE,{"disambiguationData":[OSD([sQuery(id+"F27.wireOp",EDGE,"E35.top")])]})]});}
            var sketch = newSketch(context, id + "F32", { "sketchPlane" : qUnion([Q0])});
            skCircle(sketch, "E41", {"center": v(-0.4, 40.83) * mm, "radius": 8.06 * mm});
            skSolve(sketch);
        }
        {
            var Q0;
            {var subQ4=sQuery(id+"F2.wireOp",EDGE,"E6.0.4");var subQ8=sQuery(id+"F2.wireOp",EDGE,"E6.0.0");var subQ10=makeQuery(id+"F1.opExtrude","SWEPT_FACE",FACE,{"disambiguationData":[OSD([sQuery(id+"F0.wireOp",EDGE,"E1.right")])]});var subQ11=makeQuery(id+"F5.opExtrude","SWEPT_FACE",FACE,{"disambiguationData":[OSD([sQuery(id+"F4.wireOp",EDGE,"E8.0.0")])]});var subQ15=makeQuery(id+"F1.opExtrude","SWEPT_FACE",FACE,{"disambiguationData":[OSD([sQuery(id+"F0.wireOp",EDGE,"E4.trimOffspring")])]});var subQ18=makeQuery(id+"F3.opExtrude","SWEPT_FACE",FACE,{"disambiguationData":[OSD([subQ8])]});var subQ22=makeQuery(id+"F16.opExtrude","SWEPT_FACE",FACE,{"disambiguationData":[OSD([sQuery(id+"F15.wireOp",EDGE,"E24.right")])]});var subQ24=sQuery(id+"F19.wireOp",EDGE,"E28.bottom");var subQ25=makeQuery(id+"F20.opExtrude","SWEPT_FACE",FACE,{"disambiguationData":[OSD([subQ24])]});var subQ27=makeQuery(id+"F5.opExtrude","SWEPT_FACE",FACE,{"disambiguationData":[OSD([sQuery(id+"F4.wireOp",EDGE,"E8.0.8")])]});var subQ28=makeQuery(id+"F3.opExtrude","SWEPT_FACE",FACE,{"disambiguationData":[OSD([subQ4])]});var subQ29=makeQuery(id+"F1.opExtrude","SWEPT_FACE",FACE,{"disambiguationData":[OSD([sQuery(id+"F0.wireOp",EDGE,"E1.bottom")])]});var subQ30=sQuery(id+"F19.wireOp",EDGE,"E28.left");var subQ31=sQuery(id+"F19.wireOp",EDGE,"E28.top");var subQ32=makeQuery(id+"F20.opExtrude","CAP_FACE",FACE,{"disambiguationData":[OSD([subQ24,subQ31,subQ30,sQuery(id+"F19.wireOp",EDGE,"E28.right")])],"isStart":false});var subQ37=makeQuery(id+"F9.opExtrude","SWEPT_FACE",FACE,{"disambiguationData":[OSD([sQuery(id+"F8.wireOp",EDGE,"E15.MirrorCS")])]});var subQ41=makeQuery(id+"F5.boolean.opBoolean","MERGE",FACE,{"derivedFrom":[makeQuery(id+"F3.boolean.opBoolean","MERGE",FACE,{"derivedFrom":[subQ15,subQ18]}),subQ11]});var subQ48=makeQuery(id+"F5.boolean.opBoolean","MERGE",FACE,{"derivedFrom":[makeQuery(id+"F3.boolean.opBoolean","MERGE",FACE,{"derivedFrom":[subQ29,subQ28]}),subQ27]});Q0=makeQuery(id+"F26.boolean.opBoolean","SPLIT",FACE,{"disambiguationData":[TD([subQ25])],"derivedFrom":makeQuery(id+"F24.boolean.opBoolean","SPLIT",FACE,{"disambiguationData":[TD([subQ10])],"derivedFrom":makeQuery(id+"F20.boolean.opBoolean","MERGE",FACE,{"derivedFrom":[makeQuery(id+"F16.boolean.opBoolean","SPLIT",FACE,{"disambiguationData":[TD([subQ22])],"derivedFrom":subQ48}),makeQuery(id+"F16.boolean.opBoolean","SPLIT",FACE,{"disambiguationData":[TD([makeQuery(id+"F9.opExtrude","SWEPT_FACE",FACE,{"disambiguationData":[OSD([sQuery(id+"F8.wireOp",EDGE,"E14.bottom")])]})])],"derivedFrom":subQ48}),makeQuery(id+"F16.boolean.opBoolean","SPLIT",FACE,{"disambiguationData":[TD([subQ22])],"derivedFrom":subQ41}),makeQuery(id+"F16.boolean.opBoolean","SPLIT",FACE,{"disambiguationData":[TD([subQ37])],"derivedFrom":subQ41}),subQ32]})})});}
            var sketch = newSketch(context, id + "F33", { "sketchPlane" : qUnion([Q0])});
            skCircle(sketch, "E42", {"center": v(-11.5, -187) * mm, "radius": 1.5 * mm});
            skCircle(sketch, "E43.MirrorC", {"center": v(11.5, -187) * mm, "radius": 1.5 * mm});
            skCircle(sketch, "E44", {"center": v(11.5, -90) * mm, "radius": 1.5 * mm});
            skCircle(sketch, "E45.MirrorC", {"center": v(-11.5, -90) * mm, "radius": 1.5 * mm});
            skCircle(sketch, "E46", {"center": v(-11.5, 20) * mm, "radius": 1.5 * mm});
            skCircle(sketch, "E47", {"center": v(11.5, 48.5) * mm, "radius": 1.5 * mm});
            skCircle(sketch, "E48", {"center": v(11.5, 41) * mm, "radius": 1.5 * mm});
            skCircle(sketch, "E49.MirrorC", {"center": v(11.5, 20) * mm, "radius": 1.5 * mm});
            skSolve(sketch);
        }
        {
            var Q0;
            Q0=qSketchRegion(id+"F33",true);
            var Q1;
            {var subQ9=makeQuery(id+"F1.opExtrude","SWEPT_FACE",FACE,{"disambiguationData":[OSD([sQuery(id+"F0.wireOp",EDGE,"E3.left")])]});var subQ13=makeQuery(id+"F3.opExtrude","SWEPT_FACE",FACE,{"disambiguationData":[OSD([sQuery(id+"F2.wireOp",EDGE,"E6.0.2")])]});var subQ14=makeQuery(id+"F16.opExtrude","SWEPT_FACE",FACE,{"disambiguationData":[OSD([sQuery(id+"F15.wireOp",EDGE,"E24.top")])]});var subQ15=makeQuery(id+"F1.opExtrude","SWEPT_FACE",FACE,{"disambiguationData":[OSD([sQuery(id+"F0.wireOp",EDGE,"E2.0")])]});var subQ18=makeQuery(id+"F5.opExtrude","SWEPT_FACE",FACE,{"disambiguationData":[OSD([sQuery(id+"F4.wireOp",EDGE,"E8.0.10")])]});var subQ19=makeQuery(id+"F16.opExtrude","SWEPT_FACE",FACE,{"disambiguationData":[OSD([sQuery(id+"F15.wireOp",EDGE,"E23.top")])]});var subQ25=makeQuery(id+"F16.boolean.opBoolean","MERGE",FACE,{"derivedFrom":[makeQuery(id+"F5.boolean.opBoolean","MERGE",FACE,{"derivedFrom":[makeQuery(id+"F3.boolean.opBoolean","MERGE",FACE,{"derivedFrom":[subQ15,subQ13]}),subQ18]}),subQ19,subQ14]});Q1=makeQuery(id+"F28.boolean.opBoolean","MERGE",FACE,{"derivedFrom":[makeQuery(id+"F26.boolean.opBoolean","MERGE",FACE,{"derivedFrom":[makeQuery(id+"F20.boolean.opBoolean","SPLIT",FACE,{"disambiguationData":[TD([makeQuery(id+"F20.opExtrude","SWEPT_FACE",FACE,{"disambiguationData":[OSD([sQuery(id+"F19.wireOp",EDGE,"E28.right")])]})])],"derivedFrom":subQ25}),makeQuery(id+"F20.boolean.opBoolean","SPLIT",FACE,{"disambiguationData":[TD([makeQuery(id+"F20.opExtrude","SWEPT_FACE",FACE,{"disambiguationData":[OSD([sQuery(id+"F19.wireOp",EDGE,"E28.left")])]})])],"derivedFrom":subQ25}),makeQuery(id+"F24.boolean.opBoolean","MERGE",FACE,{"derivedFrom":[makeQuery(id+"F20.boolean.opBoolean","SPLIT",FACE,{"disambiguationData":[TD([subQ9])],"derivedFrom":subQ25}),makeQuery(id+"F24.opExtrude","CAP_FACE",FACE,{"disambiguationData":[OSD([sQuery(id+"F23.wireOp",EDGE,"E33")])],"isStart":false})]}),makeQuery(id+"F26.opExtrude","CAP_FACE",FACE,{"disambiguationData":[OSD([sQuery(id+"F25.wireOp",EDGE,"E34.bottom"),sQuery(id+"F25.wireOp",EDGE,"E34.top"),sQuery(id+"F25.wireOp",EDGE,"E34.left"),sQuery(id+"F25.wireOp",EDGE,"E34.right")])],"isStart":true})]}),makeQuery(id+"F28.opExtrude","SWEPT_FACE",FACE,{"disambiguationData":[OSD([sQuery(id+"F27.wireOp",EDGE,"E35.top")])]})]});}
            extrude(context, id + "F34", {"entities" : qUnion([Q0]), "operationType" : NewBodyOperationType.REMOVE, "endBound" : BoundingType.UP_TO_SURFACE, "oppositeDirection" : true, "depth" : 25 * mm, "endBoundEntityFace" : qUnion([Q1]), "offsetDistance" : 25 * mm});
        }
        {
            var Q0;
            {var subQ2=sQuery(id+"F0.wireOp",EDGE,"E1.right");var subQ4=sQuery(id+"F4.wireOp",EDGE,"E9");var subQ5=sQuery(id+"F4.wireOp",EDGE,"E8.0.1");Q0=makeQuery(id+"F9.boolean.opBoolean","SPLIT",FACE,{"disambiguationData":[TD([makeQuery(id+"F5.opExtrude","SWEPT_FACE",FACE,{"disambiguationData":[OSD([subQ4])]})])],"derivedFrom":makeQuery(id+"F5.boolean.opBoolean","MERGE",FACE,{"derivedFrom":[makeQuery(id+"F3.boolean.opBoolean","MERGE",FACE,{"derivedFrom":[makeQuery(id+"F1.opExtrude","SWEPT_FACE",FACE,{"disambiguationData":[OSD([subQ2])]}),makeQuery(id+"F3.opExtrude","SWEPT_FACE",FACE,{"disambiguationData":[OSD([sQuery(id+"F2.wireOp",EDGE,"E6.0.11")])]})]}),makeQuery(id+"F5.opExtrude","SWEPT_FACE",FACE,{"disambiguationData":[OSD([subQ5])]})]})});}
            var sketch = newSketch(context, id + "F35", { "sketchPlane" : qUnion([Q0])});
            skLineSegment(sketch, "E50.0", {"start": v(50, 6.5) * mm, "end": v(32, 6.5) * mm});
            skLineSegment(sketch, "E51.0", {"start": v(32, 5.5) * mm, "end": v(32, 6.5) * mm});
            skLineSegment(sketch, "E52.0", {"start": v(50, 5.5) * mm, "end": v(50, 6.5) * mm});
            skLineSegment(sketch, "E53", {"start": v(50, 5.5) * mm, "end": v(32, 5.5) * mm});
            skSolve(sketch);
        }
        {
            var Q0;
            Q0=qSketchRegion(id+"F35",true);
            var Q1;
            {var subQ1=sQuery(id+"F4.wireOp",EDGE,"E8.0.11");Q1=makeQuery(id+"F16.boolean.opBoolean","SPLIT",FACE,{"disambiguationData":[TD([makeQuery(id+"F16.opExtrude","SWEPT_FACE",FACE,{"disambiguationData":[OSD([sQuery(id+"F15.wireOp",EDGE,"E23.left")])]})])],"derivedFrom":makeQuery(id+"F5.boolean.opBoolean","MERGE",FACE,{"derivedFrom":[makeQuery(id+"F3.boolean.opBoolean","MERGE",FACE,{"derivedFrom":[makeQuery(id+"F1.opExtrude","SWEPT_FACE",FACE,{"disambiguationData":[OSD([sQuery(id+"F0.wireOp",EDGE,"E3.right")])]}),makeQuery(id+"F3.opExtrude","SWEPT_FACE",FACE,{"disambiguationData":[OSD([sQuery(id+"F2.wireOp",EDGE,"E6.0.1")])]})]}),makeQuery(id+"F5.opExtrude","SWEPT_FACE",FACE,{"disambiguationData":[OSD([subQ1])]})]})});}
            extrude(context, id + "F36", {"entities" : qUnion([Q0]), "operationType" : NewBodyOperationType.ADD, "endBound" : BoundingType.UP_TO_SURFACE, "oppositeDirection" : true, "depth" : 25 * mm, "endBoundEntityFace" : qUnion([Q1]), "offsetDistance" : 25 * mm});
        }
        {
            var Q0;
            {var subQ2=sQuery(id+"F0.wireOp",EDGE,"E1.right");var subQ4=sQuery(id+"F4.wireOp",EDGE,"E9");var subQ5=sQuery(id+"F4.wireOp",EDGE,"E8.0.1");Q0=makeQuery(id+"F36.boolean.opBoolean","MERGE",FACE,{"derivedFrom":[makeQuery(id+"F9.boolean.opBoolean","SPLIT",FACE,{"disambiguationData":[TD([makeQuery(id+"F5.opExtrude","SWEPT_FACE",FACE,{"disambiguationData":[OSD([subQ4])]})])],"derivedFrom":makeQuery(id+"F5.boolean.opBoolean","MERGE",FACE,{"derivedFrom":[makeQuery(id+"F3.boolean.opBoolean","MERGE",FACE,{"derivedFrom":[makeQuery(id+"F1.opExtrude","SWEPT_FACE",FACE,{"disambiguationData":[OSD([subQ2])]}),makeQuery(id+"F3.opExtrude","SWEPT_FACE",FACE,{"disambiguationData":[OSD([sQuery(id+"F2.wireOp",EDGE,"E6.0.11")])]})]}),makeQuery(id+"F5.opExtrude","SWEPT_FACE",FACE,{"disambiguationData":[OSD([subQ5])]})]})}),makeQuery(id+"F36.opExtrude","CAP_FACE",FACE,{"disambiguationData":[OSD([sQuery(id+"F35.wireOp",EDGE,"E50.0"),sQuery(id+"F35.wireOp",EDGE,"E51.0"),sQuery(id+"F35.wireOp",EDGE,"E52.0"),sQuery(id+"F35.wireOp",EDGE,"E53")])],"isStart":true})]});}
            var sketch = newSketch(context, id + "F37", { "sketchPlane" : qUnion([Q0])});
            skCircle(sketch, "E54", {"center": v(41, 6.25) * mm, "radius": 0.75 * mm});
            skLineSegment(sketch, "E55", {"start": v(43.25, 2.5) * mm, "end": v(43.25, 5.5) * mm});
            skLineSegment(sketch, "E56", {"start": v(43.25, 5.5) * mm, "end": v(34.1, 5.5) * mm});
            skCircle(sketch, "E57", {"center": v(48.5, 6.25) * mm, "radius": 0.75 * mm});
            skSolve(sketch);
        }
        {
            var Q0;
            Q0=qSketchRegion(id+"F37",true);
            extrude(context, id + "F38", {"entities" : qUnion([Q0]), "operationType" : NewBodyOperationType.REMOVE, "endBound" : BoundingType.THROUGH_ALL, "oppositeDirection" : true, "depth" : 25 * mm, "offsetDistance" : 25 * mm});
        }
        {
            var Q0;
            {var subQ0=makeQuery(id+"F5.opExtrude","SWEPT_FACE",FACE,{"disambiguationData":[OSD([sQuery(id+"F4.wireOp",EDGE,"E8.0.8")])]});var subQ9=makeQuery(id+"F1.opExtrude","SWEPT_FACE",FACE,{"disambiguationData":[OSD([sQuery(id+"F0.wireOp",EDGE,"E1.bottom")])]});var subQ10=sQuery(id+"F2.wireOp",EDGE,"E6.0.4");var subQ11=makeQuery(id+"F3.opExtrude","SWEPT_FACE",FACE,{"disambiguationData":[OSD([subQ10])]});var subQ12=makeQuery(id+"F1.opExtrude","SWEPT_FACE",FACE,{"disambiguationData":[OSD([sQuery(id+"F0.wireOp",EDGE,"E3.left")])]});var subQ13=makeQuery(id+"F1.opExtrude","SWEPT_FACE",FACE,{"disambiguationData":[OSD([sQuery(id+"F0.wireOp",EDGE,"E1.left")])]});var subQ21=makeQuery(id+"F9.opExtrude","SWEPT_FACE",FACE,{"disambiguationData":[OSD([sQuery(id+"F8.wireOp",EDGE,"E14.bottom")])]});var subQ25=sQuery(id+"F19.wireOp",EDGE,"E28.right");var subQ28=sQuery(id+"F2.wireOp",EDGE,"E6.0.0");var subQ30=makeQuery(id+"F16.opExtrude","SWEPT_FACE",FACE,{"disambiguationData":[OSD([sQuery(id+"F15.wireOp",EDGE,"E24.right")])]});var subQ31=sQuery(id+"F19.wireOp",EDGE,"E28.bottom");var subQ32=sQuery(id+"F19.wireOp",EDGE,"E28.top");var subQ39=makeQuery(id+"F5.boolean.opBoolean","MERGE",FACE,{"derivedFrom":[makeQuery(id+"F3.boolean.opBoolean","MERGE",FACE,{"derivedFrom":[makeQuery(id+"F1.opExtrude","SWEPT_FACE",FACE,{"disambiguationData":[OSD([sQuery(id+"F0.wireOp",EDGE,"E4.trimOffspring")])]}),makeQuery(id+"F3.opExtrude","SWEPT_FACE",FACE,{"disambiguationData":[OSD([subQ28])]})]}),makeQuery(id+"F5.opExtrude","SWEPT_FACE",FACE,{"disambiguationData":[OSD([sQuery(id+"F4.wireOp",EDGE,"E8.0.0")])]})]});var subQ40=makeQuery(id+"F5.boolean.opBoolean","MERGE",FACE,{"derivedFrom":[makeQuery(id+"F3.boolean.opBoolean","MERGE",FACE,{"derivedFrom":[subQ9,subQ11]}),subQ0]});Q0=makeQuery(id+"F26.boolean.opBoolean","SPLIT",FACE,{"disambiguationData":[TD([subQ12])],"derivedFrom":makeQuery(id+"F24.boolean.opBoolean","SPLIT",FACE,{"disambiguationData":[TD([subQ13])],"derivedFrom":makeQuery(id+"F20.boolean.opBoolean","MERGE",FACE,{"derivedFrom":[makeQuery(id+"F16.boolean.opBoolean","SPLIT",FACE,{"disambiguationData":[TD([subQ30])],"derivedFrom":subQ40}),makeQuery(id+"F16.boolean.opBoolean","SPLIT",FACE,{"disambiguationData":[TD([subQ21])],"derivedFrom":subQ40}),makeQuery(id+"F16.boolean.opBoolean","SPLIT",FACE,{"disambiguationData":[TD([subQ30])],"derivedFrom":subQ39}),makeQuery(id+"F16.boolean.opBoolean","SPLIT",FACE,{"disambiguationData":[TD([makeQuery(id+"F9.opExtrude","SWEPT_FACE",FACE,{"disambiguationData":[OSD([sQuery(id+"F8.wireOp",EDGE,"E15.MirrorCS")])]})])],"derivedFrom":subQ39}),makeQuery(id+"F20.opExtrude","CAP_FACE",FACE,{"disambiguationData":[OSD([subQ31,subQ32,sQuery(id+"F19.wireOp",EDGE,"E28.left"),subQ25])],"isStart":false})]})})});}
            var sketch = newSketch(context, id + "F39", { "sketchPlane" : qUnion([Q0])});
            skCircle(sketch, "E58.0", {"center": v(-11.5, -187) * mm, "radius": 1.5 * mm});
            skCircle(sketch, "E59.0", {"center": v(11.5, -187) * mm, "radius": 1.5 * mm});
            skCircle(sketch, "E60.0", {"center": v(-11.5, -90) * mm, "radius": 1.5 * mm});
            skCircle(sketch, "E61.0", {"center": v(11.5, -90) * mm, "radius": 1.5 * mm});
            skCircle(sketch, "E62.0", {"center": v(-11.5, 20) * mm, "radius": 1.5 * mm});
            skCircle(sketch, "E63.0", {"center": v(11.5, 20) * mm, "radius": 1.5 * mm});
            skSolve(sketch);
        }
        {
            var Q0;
            Q0=qSketchRegion(id+"F39",true);
            extrude(context, id + "F40", {"entities" : qUnion([Q0]), "operationType" : NewBodyOperationType.REMOVE, "oppositeDirection" : true, "depth" : 5 * mm, "offsetDistance" : 25 * mm});
        }
        {
            var Q0;
            {var subQ2=makeQuery(id+"F3.opExtrude","SWEPT_FACE",FACE,{"disambiguationData":[OSD([sQuery(id+"F2.wireOp",EDGE,"E6.0.5")])]});var subQ13=sQuery(id+"F0.wireOp",EDGE,"E1.left");var subQ14=makeQuery(id+"F1.opExtrude","SWEPT_FACE",FACE,{"disambiguationData":[OSD([subQ13])]});var subQ15=sQuery(id+"F4.wireOp",EDGE,"E8.0.7");var subQ16=makeQuery(id+"F5.opExtrude","SWEPT_FACE",FACE,{"disambiguationData":[OSD([subQ15])]});var subQ24=sQuery(id+"F4.wireOp",EDGE,"E9");var subQ25=makeQuery(id+"F5.opExtrude","SWEPT_FACE",FACE,{"disambiguationData":[OSD([subQ24])]});var subQ28=sQuery(id+"F0.wireOp",EDGE,"E0.bottom");var subQ30=makeQuery(id+"F1.opExtrude","SWEPT_FACE",FACE,{"disambiguationData":[OSD([subQ28])]});Q0=makeQuery(id+"F30.boolean.opBoolean","SPLIT",FACE,{"disambiguationData":[TD([subQ30])],"derivedFrom":makeQuery(id+"F9.boolean.opBoolean","SPLIT",FACE,{"disambiguationData":[TD([subQ25])],"derivedFrom":makeQuery(id+"F5.boolean.opBoolean","MERGE",FACE,{"derivedFrom":[makeQuery(id+"F3.boolean.opBoolean","MERGE",FACE,{"derivedFrom":[subQ14,subQ2]}),subQ16]})})});}
            var sketch = newSketch(context, id + "F41", { "sketchPlane" : qUnion([Q0])});
            skCircle(sketch, "E64", {"center": v(-25, 6) * mm, "radius": 1.5 * mm});
            skPoint(sketch, "E65", {"position": v(-28.5, 6) * mm});
            skSolve(sketch);
        }
        {
            var Q0;
            Q0=qSketchRegion(id+"F41",true);
            extrude(context, id + "F42", {"entities" : qUnion([Q0]), "operationType" : NewBodyOperationType.REMOVE, "oppositeDirection" : true, "depth" : 5 * mm, "offsetDistance" : 25 * mm});
        }
        {
            var Q0;
            {var subQ4=sQuery(id+"F2.wireOp",EDGE,"E6.0.4");var subQ8=sQuery(id+"F2.wireOp",EDGE,"E6.0.0");var subQ10=makeQuery(id+"F1.opExtrude","SWEPT_FACE",FACE,{"disambiguationData":[OSD([sQuery(id+"F0.wireOp",EDGE,"E1.right")])]});var subQ11=makeQuery(id+"F5.opExtrude","SWEPT_FACE",FACE,{"disambiguationData":[OSD([sQuery(id+"F4.wireOp",EDGE,"E8.0.0")])]});var subQ15=makeQuery(id+"F1.opExtrude","SWEPT_FACE",FACE,{"disambiguationData":[OSD([sQuery(id+"F0.wireOp",EDGE,"E4.trimOffspring")])]});var subQ18=makeQuery(id+"F3.opExtrude","SWEPT_FACE",FACE,{"disambiguationData":[OSD([subQ8])]});var subQ22=makeQuery(id+"F16.opExtrude","SWEPT_FACE",FACE,{"disambiguationData":[OSD([sQuery(id+"F15.wireOp",EDGE,"E24.right")])]});var subQ24=sQuery(id+"F19.wireOp",EDGE,"E28.bottom");var subQ25=makeQuery(id+"F20.opExtrude","SWEPT_FACE",FACE,{"disambiguationData":[OSD([subQ24])]});var subQ27=makeQuery(id+"F5.opExtrude","SWEPT_FACE",FACE,{"disambiguationData":[OSD([sQuery(id+"F4.wireOp",EDGE,"E8.0.8")])]});var subQ28=makeQuery(id+"F3.opExtrude","SWEPT_FACE",FACE,{"disambiguationData":[OSD([subQ4])]});var subQ29=makeQuery(id+"F1.opExtrude","SWEPT_FACE",FACE,{"disambiguationData":[OSD([sQuery(id+"F0.wireOp",EDGE,"E1.bottom")])]});var subQ30=sQuery(id+"F19.wireOp",EDGE,"E28.left");var subQ31=sQuery(id+"F19.wireOp",EDGE,"E28.top");var subQ32=makeQuery(id+"F20.opExtrude","CAP_FACE",FACE,{"disambiguationData":[OSD([subQ24,subQ31,subQ30,sQuery(id+"F19.wireOp",EDGE,"E28.right")])],"isStart":false});var subQ37=makeQuery(id+"F9.opExtrude","SWEPT_FACE",FACE,{"disambiguationData":[OSD([sQuery(id+"F8.wireOp",EDGE,"E15.MirrorCS")])]});var subQ41=makeQuery(id+"F5.boolean.opBoolean","MERGE",FACE,{"derivedFrom":[makeQuery(id+"F3.boolean.opBoolean","MERGE",FACE,{"derivedFrom":[subQ15,subQ18]}),subQ11]});var subQ48=makeQuery(id+"F5.boolean.opBoolean","MERGE",FACE,{"derivedFrom":[makeQuery(id+"F3.boolean.opBoolean","MERGE",FACE,{"derivedFrom":[subQ29,subQ28]}),subQ27]});Q0=makeQuery(id+"F26.boolean.opBoolean","SPLIT",FACE,{"disambiguationData":[TD([subQ25])],"derivedFrom":makeQuery(id+"F24.boolean.opBoolean","SPLIT",FACE,{"disambiguationData":[TD([subQ10])],"derivedFrom":makeQuery(id+"F20.boolean.opBoolean","MERGE",FACE,{"derivedFrom":[makeQuery(id+"F16.boolean.opBoolean","SPLIT",FACE,{"disambiguationData":[TD([subQ22])],"derivedFrom":subQ48}),makeQuery(id+"F16.boolean.opBoolean","SPLIT",FACE,{"disambiguationData":[TD([makeQuery(id+"F9.opExtrude","SWEPT_FACE",FACE,{"disambiguationData":[OSD([sQuery(id+"F8.wireOp",EDGE,"E14.bottom")])]})])],"derivedFrom":subQ48}),makeQuery(id+"F16.boolean.opBoolean","SPLIT",FACE,{"disambiguationData":[TD([subQ22])],"derivedFrom":subQ41}),makeQuery(id+"F16.boolean.opBoolean","SPLIT",FACE,{"disambiguationData":[TD([subQ37])],"derivedFrom":subQ41}),subQ32]})})});}
            var sketch = newSketch(context, id + "F43", { "sketchPlane" : qUnion([Q0])});
            skLineSegment(sketch, "E66.bottom", {"start": v(7.5, -190) * mm, "end": v(-7.5, -190) * mm});
            skLineSegment(sketch, "E66.top", {"start": v(7.5, -175.93) * mm, "end": v(-7.5, -175.93) * mm});
            skLineSegment(sketch, "E66.left", {"start": v(7.5, -190) * mm, "end": v(7.5, -175.93) * mm});
            skLineSegment(sketch, "E66.right", {"start": v(-7.5, -190) * mm, "end": v(-7.5, -175.93) * mm});
            skSolve(sketch);
        }
        {
            var Q0;
            Q0=qSketchRegion(id+"F43",true);
            var Q1;
            {var subQ9=makeQuery(id+"F1.opExtrude","SWEPT_FACE",FACE,{"disambiguationData":[OSD([sQuery(id+"F0.wireOp",EDGE,"E3.left")])]});var subQ13=makeQuery(id+"F3.opExtrude","SWEPT_FACE",FACE,{"disambiguationData":[OSD([sQuery(id+"F2.wireOp",EDGE,"E6.0.2")])]});var subQ14=makeQuery(id+"F16.opExtrude","SWEPT_FACE",FACE,{"disambiguationData":[OSD([sQuery(id+"F15.wireOp",EDGE,"E24.top")])]});var subQ15=makeQuery(id+"F1.opExtrude","SWEPT_FACE",FACE,{"disambiguationData":[OSD([sQuery(id+"F0.wireOp",EDGE,"E2.0")])]});var subQ18=makeQuery(id+"F5.opExtrude","SWEPT_FACE",FACE,{"disambiguationData":[OSD([sQuery(id+"F4.wireOp",EDGE,"E8.0.10")])]});var subQ19=makeQuery(id+"F16.opExtrude","SWEPT_FACE",FACE,{"disambiguationData":[OSD([sQuery(id+"F15.wireOp",EDGE,"E23.top")])]});var subQ25=makeQuery(id+"F16.boolean.opBoolean","MERGE",FACE,{"derivedFrom":[makeQuery(id+"F5.boolean.opBoolean","MERGE",FACE,{"derivedFrom":[makeQuery(id+"F3.boolean.opBoolean","MERGE",FACE,{"derivedFrom":[subQ15,subQ13]}),subQ18]}),subQ19,subQ14]});Q1=makeQuery(id+"F28.boolean.opBoolean","MERGE",FACE,{"derivedFrom":[makeQuery(id+"F26.boolean.opBoolean","MERGE",FACE,{"derivedFrom":[makeQuery(id+"F20.boolean.opBoolean","SPLIT",FACE,{"disambiguationData":[TD([makeQuery(id+"F20.opExtrude","SWEPT_FACE",FACE,{"disambiguationData":[OSD([sQuery(id+"F19.wireOp",EDGE,"E28.right")])]})])],"derivedFrom":subQ25}),makeQuery(id+"F20.boolean.opBoolean","SPLIT",FACE,{"disambiguationData":[TD([makeQuery(id+"F20.opExtrude","SWEPT_FACE",FACE,{"disambiguationData":[OSD([sQuery(id+"F19.wireOp",EDGE,"E28.left")])]})])],"derivedFrom":subQ25}),makeQuery(id+"F24.boolean.opBoolean","MERGE",FACE,{"derivedFrom":[makeQuery(id+"F20.boolean.opBoolean","SPLIT",FACE,{"disambiguationData":[TD([subQ9])],"derivedFrom":subQ25}),makeQuery(id+"F24.opExtrude","CAP_FACE",FACE,{"disambiguationData":[OSD([sQuery(id+"F23.wireOp",EDGE,"E33")])],"isStart":false})]}),makeQuery(id+"F26.opExtrude","CAP_FACE",FACE,{"disambiguationData":[OSD([sQuery(id+"F25.wireOp",EDGE,"E34.bottom"),sQuery(id+"F25.wireOp",EDGE,"E34.top"),sQuery(id+"F25.wireOp",EDGE,"E34.left"),sQuery(id+"F25.wireOp",EDGE,"E34.right")])],"isStart":true})]}),makeQuery(id+"F28.opExtrude","SWEPT_FACE",FACE,{"disambiguationData":[OSD([sQuery(id+"F27.wireOp",EDGE,"E35.top")])]})]});}
            extrude(context, id + "F44", {"entities" : qUnion([Q0]), "operationType" : NewBodyOperationType.REMOVE, "endBound" : BoundingType.UP_TO_SURFACE, "oppositeDirection" : true, "depth" : 25 * mm, "endBoundEntityFace" : qUnion([Q1]), "offsetDistance" : 25 * mm});
        }
        {
            var Q0;
            {var subQ2=sQuery(id+"F4.wireOp",EDGE,"E8.0.0");Q0=makeQuery(id+"F16.boolean.opBoolean","SPLIT",FACE,{"disambiguationData":[TD([makeQuery(id+"F16.opExtrude","SWEPT_FACE",FACE,{"disambiguationData":[OSD([sQuery(id+"F15.wireOp",EDGE,"E23.left")])]})])],"derivedFrom":makeQuery(id+"F5.boolean.opBoolean","MERGE",FACE,{"derivedFrom":[makeQuery(id+"F3.boolean.opBoolean","MERGE",FACE,{"derivedFrom":[makeQuery(id+"F1.opExtrude","SWEPT_FACE",FACE,{"disambiguationData":[OSD([sQuery(id+"F0.wireOp",EDGE,"E4.trimOffspring")])]}),makeQuery(id+"F3.opExtrude","SWEPT_FACE",FACE,{"disambiguationData":[OSD([sQuery(id+"F2.wireOp",EDGE,"E6.0.0")])]})]}),makeQuery(id+"F5.opExtrude","SWEPT_FACE",FACE,{"disambiguationData":[OSD([subQ2])]})]})});}
            var sketch = newSketch(context, id + "F45", { "sketchPlane" : qUnion([Q0])});
            skCircle(sketch, "E67.0", {"center": v(11.5, 41) * mm, "radius": 1.5 * mm});
            skCircle(sketch, "E68.0", {"center": v(11.5, 48.5) * mm, "radius": 1.5 * mm});
            skSolve(sketch);
        }
        {
            var Q0;
            Q0=qSketchRegion(id+"F45",true);
            extrude(context, id + "F46", {"entities" : qUnion([Q0]), "operationType" : NewBodyOperationType.REMOVE, "oppositeDirection" : true, "depth" : 4 * mm, "offsetDistance" : 25 * mm});
        }
    });
